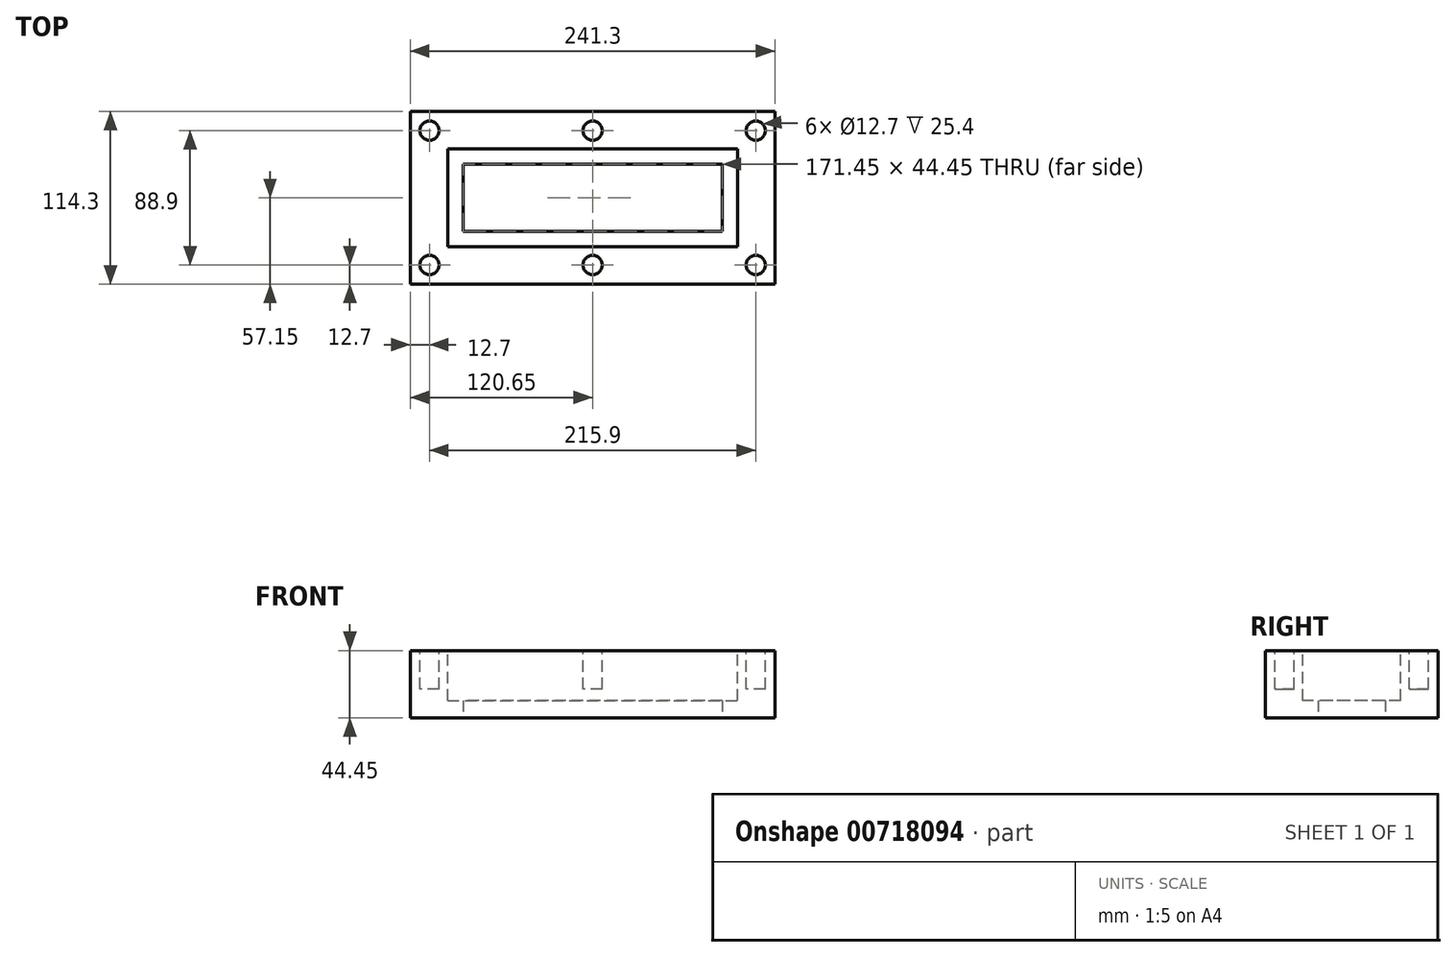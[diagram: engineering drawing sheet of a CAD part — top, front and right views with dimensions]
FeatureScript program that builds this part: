
annotation { "Feature Type Name" : "Feature", "Feature Type Description" : "" }
export const myFeature = defineFeature(function(context is Context, id is Id, definition is map)
    precondition{}
    {
        {
            var Q0;
            Q0=qCreatedBy(makeId("Top.planeOp"),FACE);
            var sketch = newSketch(context, id + "F0", { "sketchPlane" : qUnion([Q0])});
            skLineSegment(sketch, "E0.bottom", {"start": v(-120.65, 57.15) * mm, "end": v(120.65, 57.15) * mm});
            skLineSegment(sketch, "E0.top", {"start": v(-120.65, -57.15) * mm, "end": v(120.65, -57.15) * mm});
            skLineSegment(sketch, "E0.left", {"start": v(-120.65, 57.15) * mm, "end": v(-120.65, -57.15) * mm});
            skLineSegment(sketch, "E0.right", {"start": v(120.65, 57.15) * mm, "end": v(120.65, -57.15) * mm});
            skPoint(sketch, "E0.middle", {"position": v(0, 0) * mm});
            skSolve(sketch);
        }
        {
            var Q0;
            Q0=makeQuery(id+"F0.imprint","IMPRINT",FACE,{"disambiguationData":[TD([[makeQuery(id+"F0.imprint","IMPRINT",EDGE,{"derivedFrom":sQuery(id+"F0.wireOp",EDGE,"E0.bottom")}),-1.0]])]});
            extrude(context, id + "F1", {"entities" : qUnion([Q0]), "depth" : 44.45 * mm, "offsetDistance" : 25.4 * mm});
        }
        {
            var Q0;
            Q0=makeQuery(id+"F1.opExtrude","CAP_FACE",FACE,{"disambiguationData":[OSD([sQuery(id+"F0.wireOp",EDGE,"E0.bottom"),sQuery(id+"F0.wireOp",EDGE,"E0.top"),sQuery(id+"F0.wireOp",EDGE,"E0.left"),sQuery(id+"F0.wireOp",EDGE,"E0.right")])],"isStart":false});
            var sketch = newSketch(context, id + "F2", { "sketchPlane" : qUnion([Q0])});
            skLineSegment(sketch, "E1.bottom", {"start": v(-95.89, 32.39) * mm, "end": v(95.89, 32.39) * mm});
            skLineSegment(sketch, "E1.top", {"start": v(-95.89, -32.39) * mm, "end": v(95.89, -32.39) * mm});
            skLineSegment(sketch, "E1.left", {"start": v(-95.89, 32.39) * mm, "end": v(-95.89, -32.39) * mm});
            skLineSegment(sketch, "E1.right", {"start": v(95.89, 32.39) * mm, "end": v(95.89, -32.39) * mm});
            skPoint(sketch, "E1.middle", {"position": v(0, 0) * mm});
            skSolve(sketch);
        }
        {
            var Q0;
            Q0=makeQuery(id+"F2.imprint","IMPRINT",FACE,{"disambiguationData":[TD([[makeQuery(id+"F2.imprint","IMPRINT",EDGE,{"derivedFrom":sQuery(id+"F2.wireOp",EDGE,"E1.bottom")}),-1.0]])]});
            extrude(context, id + "F3", {"entities" : qUnion([Q0]), "operationType" : NewBodyOperationType.REMOVE, "oppositeDirection" : true, "depth" : 33.02 * mm, "offsetDistance" : 25.4 * mm});
        }
        {
            var Q0;
            Q0=makeQuery(id+"F1.opExtrude","CAP_FACE",FACE,{"disambiguationData":[OSD([sQuery(id+"F0.wireOp",EDGE,"E0.bottom"),sQuery(id+"F0.wireOp",EDGE,"E0.top"),sQuery(id+"F0.wireOp",EDGE,"E0.left"),sQuery(id+"F0.wireOp",EDGE,"E0.right")])],"isStart":true});
            var sketch = newSketch(context, id + "F4", { "sketchPlane" : qUnion([Q0])});
            skLineSegment(sketch, "E2.bottom", {"start": v(-85.73, 22.23) * mm, "end": v(85.73, 22.23) * mm});
            skLineSegment(sketch, "E2.top", {"start": v(-85.73, -22.23) * mm, "end": v(85.73, -22.23) * mm});
            skLineSegment(sketch, "E2.left", {"start": v(-85.73, 22.23) * mm, "end": v(-85.73, -22.23) * mm});
            skLineSegment(sketch, "E2.right", {"start": v(85.73, 22.23) * mm, "end": v(85.73, -22.23) * mm});
            skPoint(sketch, "E2.middle", {"position": v(0, 0) * mm});
            skSolve(sketch);
        }
        {
            var Q0;
            Q0=makeQuery(id+"F4.imprint","IMPRINT",FACE,{"disambiguationData":[TD([[makeQuery(id+"F4.imprint","IMPRINT",EDGE,{"derivedFrom":sQuery(id+"F4.wireOp",EDGE,"E2.bottom")}),-1.0]])]});
            extrude(context, id + "F5", {"entities" : qUnion([Q0]), "operationType" : NewBodyOperationType.REMOVE, "oppositeDirection" : true, "depth" : 25.4 * mm, "offsetDistance" : 25.4 * mm});
        }
        {
            var Q0;
            Q0=makeQuery(id+"F1.opExtrude","CAP_FACE",FACE,{"disambiguationData":[OSD([sQuery(id+"F0.wireOp",EDGE,"E0.bottom"),sQuery(id+"F0.wireOp",EDGE,"E0.top"),sQuery(id+"F0.wireOp",EDGE,"E0.left"),sQuery(id+"F0.wireOp",EDGE,"E0.right")])],"isStart":false});
            var sketch = newSketch(context, id + "F6", { "sketchPlane" : qUnion([Q0])});
            skPoint(sketch, "E3.middle", {"position": v(0, 0) * mm});
            skCircle(sketch, "E4", {"center": v(-107.95, 44.45) * mm, "radius": 6.35 * mm});
            skCircle(sketch, "E5", {"center": v(-107.95, -44.45) * mm, "radius": 6.35 * mm});
            skCircle(sketch, "E6", {"center": v(107.95, -44.45) * mm, "radius": 6.35 * mm});
            skCircle(sketch, "E7", {"center": v(107.95, 44.45) * mm, "radius": 6.35 * mm});
            skCircle(sketch, "E8", {"center": v(0, 44.45) * mm, "radius": 6.35 * mm});
            skCircle(sketch, "E9", {"center": v(0, -44.45) * mm, "radius": 6.35 * mm});
            skSolve(sketch);
        }
        {
            var Q0;
            Q0=makeQuery(id+"F6.imprint","IMPRINT",FACE,{"disambiguationData":[TD([[makeQuery(id+"F6.imprint","IMPRINT",EDGE,{"derivedFrom":sQuery(id+"F6.wireOp",EDGE,"E4")}),1.0]])]});
            var Q1;
            Q1=makeQuery(id+"F6.imprint","IMPRINT",FACE,{"disambiguationData":[TD([[makeQuery(id+"F6.imprint","IMPRINT",EDGE,{"derivedFrom":sQuery(id+"F6.wireOp",EDGE,"E8")}),1.0]])]});
            var Q2;
            Q2=makeQuery(id+"F6.imprint","IMPRINT",FACE,{"disambiguationData":[TD([[makeQuery(id+"F6.imprint","IMPRINT",EDGE,{"derivedFrom":sQuery(id+"F6.wireOp",EDGE,"E7")}),1.0]])]});
            var Q3;
            Q3=makeQuery(id+"F6.imprint","IMPRINT",FACE,{"disambiguationData":[TD([[makeQuery(id+"F6.imprint","IMPRINT",EDGE,{"derivedFrom":sQuery(id+"F6.wireOp",EDGE,"E6")}),1.0]])]});
            var Q4;
            Q4=makeQuery(id+"F6.imprint","IMPRINT",FACE,{"disambiguationData":[TD([[makeQuery(id+"F6.imprint","IMPRINT",EDGE,{"derivedFrom":sQuery(id+"F6.wireOp",EDGE,"E9")}),1.0]])]});
            var Q5;
            Q5=makeQuery(id+"F6.imprint","IMPRINT",FACE,{"disambiguationData":[TD([[makeQuery(id+"F6.imprint","IMPRINT",EDGE,{"derivedFrom":sQuery(id+"F6.wireOp",EDGE,"E5")}),1.0]])]});
            extrude(context, id + "F7", {"entities" : qUnion([Q0, Q1, Q2, Q3, Q4, Q5]), "operationType" : NewBodyOperationType.REMOVE, "oppositeDirection" : true, "depth" : 25.4 * mm, "offsetDistance" : 25.4 * mm});
        }
    });
